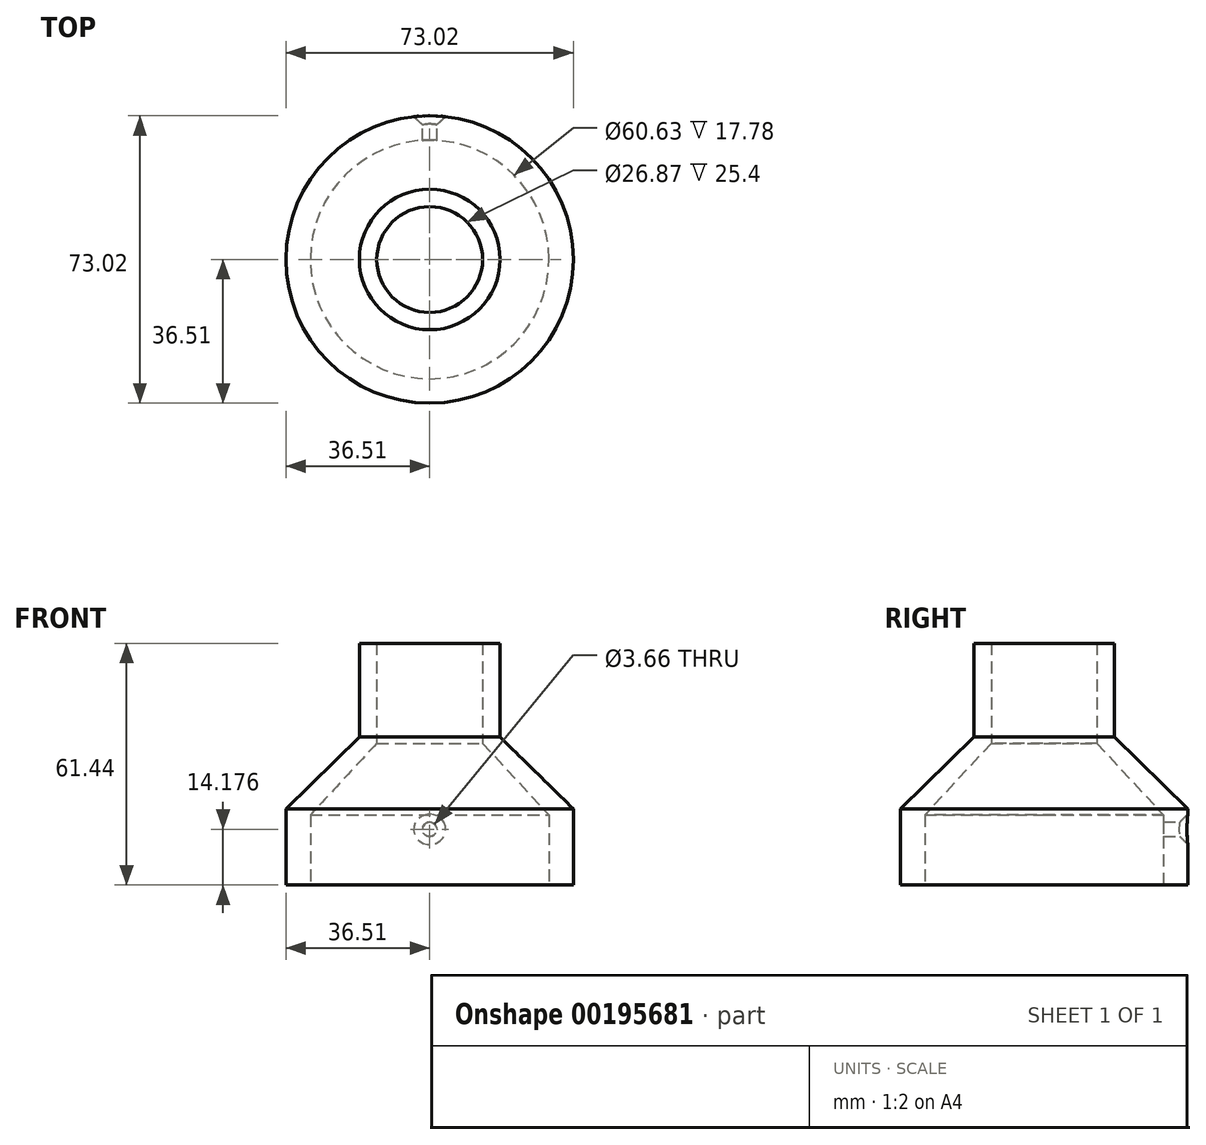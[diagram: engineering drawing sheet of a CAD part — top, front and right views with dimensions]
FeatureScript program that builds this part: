
annotation { "Feature Type Name" : "Feature", "Feature Type Description" : "" }
export const myFeature = defineFeature(function(context is Context, id is Id, definition is map)
    precondition{}
    {
        {
            var Q0;
            Q0=qCreatedBy(makeId("Top.planeOp"),FACE);
            var sketch = newSketch(context, id + "F0", { "sketchPlane" : qUnion([Q0])});
            skCircle(sketch, "E0", {"center": v(0, 0) * mm, "radius": 36.51 * mm});
            skSolve(sketch);
        }
        {
            var Q0;
            Q0 = qSketchRegion(id + "F0", true);
            extrude(context, id + "F1", {"entities" : qUnion([Q0]), "depth" : 39.69 * mm, "offsetDistance" : 25.4 * mm});
        }
        {
            var Q0;
            Q0=makeQuery(id+"F1.opExtrude","CAP_FACE",FACE,{"disambiguationData":[OSD([sQuery(id+"F0.wireOp",EDGE,"E0")])],"isStart":false});
            cPlane(context, id + "F2", {"entities" : qUnion([Q0]), "cplaneType" : CPlaneType.OFFSET, "offset" : 18.26 * mm, "width" : 152.4 * mm, "height" : 152.4 * mm});
        }
        {
            var Q0;
            Q0=qCreatedBy(id+"F2.planeOp",FACE);
            var sketch = newSketch(context, id + "F3", { "sketchPlane" : qUnion([Q0])});
            skCircle(sketch, "E1", {"center": v(0, 0) * mm, "radius": 17.86 * mm});
            skSolve(sketch);
        }
        {
            var Q0;
            Q0=makeQuery(id+"F1.opExtrude","CAP_FACE",FACE,{"disambiguationData":[OSD([sQuery(id+"F0.wireOp",EDGE,"E0")])],"isStart":false});
            var Q1;
            Q1=makeQuery(id+"F3.imprint","IMPRINT",FACE,{"disambiguationData":[TD([[makeQuery(id+"F3.imprint","IMPRINT",EDGE,{"derivedFrom":sQuery(id+"F3.wireOp",EDGE,"E1")}),1.0]])]});
            loft(context, id + "F4", {"operationType" : NewBodyOperationType.ADD, "sheetProfilesArray" : [{ "sheetProfileEntities" : qUnion([Q0]) }, { "sheetProfileEntities" : qUnion([Q1]) }]});
        }
        {
            var Q0;
            Q0=makeQuery(id+"F1.opExtrude","CAP_FACE",FACE,{"disambiguationData":[OSD([sQuery(id+"F0.wireOp",EDGE,"E0")])],"isStart":true});
            cPlane(context, id + "F5", {"entities" : qUnion([Q0]), "cplaneType" : CPlaneType.OFFSET, "offset" : 81.76 * mm, "oppositeDirection" : true, "width" : 152.4 * mm, "height" : 152.4 * mm});
        }
        {
            var Q0;
            Q0=makeQuery(id+"F4.opLoft","CAP_FACE",FACE,{"disambiguationData":[OSD([makeQuery(id+"F3.imprint","IMPRINT",FACE,{"disambiguationData":[TD([[makeQuery(id+"F3.imprint","IMPRINT",EDGE,{"derivedFrom":sQuery(id+"F3.wireOp",EDGE,"E1")}),1.0]])]})])],"isStart":true});
            var Q1;
            Q1=qCreatedBy(id+"F5.planeOp",FACE);
            extrude(context, id + "F6", {"entities" : qUnion([Q0]), "operationType" : NewBodyOperationType.ADD, "endBound" : BoundingType.UP_TO_SURFACE, "depth" : 25.4 * mm, "endBoundEntityFace" : qUnion([Q1]), "offsetDistance" : 25.4 * mm});
        }
        {
            var Q0;
            Q0=qCreatedBy(makeId("Front.planeOp"),FACE);
            var sketch = newSketch(context, id + "F7", { "sketchPlane" : qUnion([Q0])});
            skLineSegment(sketch, "E2.bottom", {"start": v(0, 81.76) * mm, "end": v(13.44, 81.76) * mm});
            skLineSegment(sketch, "E2.right", {"start": v(13.44, 81.76) * mm, "end": v(13.44, 56.36) * mm});
            skPoint(sketch, "E3", {"position": v(0, 81.76) * mm});
            skLineSegment(sketch, "E4", {"start": v(0, 81.76) * mm, "end": v(0, 0) * mm});
            skPoint(sketch, "E2.left.start.orphan", {"position": v(-13.44, 81.76) * mm});
            skLineSegment(sketch, "E5", {"start": v(0, 0) * mm, "end": v(30.31, 0) * mm});
            skLineSegment(sketch, "E6", {"start": v(30.31, 0) * mm, "end": v(30.31, 38.1) * mm});
            skLineSegment(sketch, "E7", {"start": v(13.44, 56.36) * mm, "end": v(30.31, 38.1) * mm});
            skSolve(sketch);
        }
        {
            var Q0;
            Q0 = qSketchRegion(id + "F7", true);
            var Q1;
            Q1 = qConstructionFilter(qBodyType(qCreatedBy(id + "F7" ,EDGE), BodyType.WIRE), ConstructionObject.NO);
            var Q2;
            Q2=sQuery(id+"F7.wireOp",EDGE,"E4");
            revolve(context, id + "F8", {"operationType" : NewBodyOperationType.REMOVE, "surfaceOperationType" : NewSurfaceOperationType.NEW, "entities" : qUnion([Q0]), "surfaceEntities" : qUnion([Q1]), "axis" : qUnion([Q2]), "revolveType" : RevolveType.FULL, "oppositeDirection" : true});
        }
        {
            var Q0;
            Q0=makeQuery(id+"F1.opExtrude","CAP_FACE",FACE,{"disambiguationData":[OSD([sQuery(id+"F0.wireOp",EDGE,"E0")])],"isStart":true});
            extrude(context, id + "F9", {"entities" : qUnion([Q0]), "operationType" : NewBodyOperationType.REMOVE, "oppositeDirection" : true, "depth" : 20.32 * mm, "offsetDistance" : 25.4 * mm});
        }
        {
            var Q0;
            Q0=qCreatedBy(makeId("Front.planeOp"),FACE);
            var sketch = newSketch(context, id + "F10", { "sketchPlane" : qUnion([Q0])});
            skPoint(sketch, "E8", {"position": v(0, 31.5) * mm});
            skSolve(sketch);
        }
        {
            var Q0;
            Q0=makeQuery(id+"F9.boolean.opBoolean","COPY",FACE,{"derivedFrom":makeQuery(id+"F9.opExtrude","CAP_FACE",FACE,{"disambiguationData":[OSD([sQuery(id+"F0.wireOp",EDGE,"E0")])],"isStart":false})});
            var sketch = newSketch(context, id + "F11", { "sketchPlane" : qUnion([Q0])});
            skPoint(sketch, "E9", {"position": v(0, -36.51) * mm});
            skSolve(sketch);
        }
        {
            var Q0;
            Q0=qCreatedBy(makeId("Front.planeOp"),FACE);
            var Q1;
            Q1=sQuery(id+"F11.wireOp",VERTEX,"E9");
            cPlane(context, id + "F12", {"entities" : qUnion([Q0, Q1]), "cplaneType" : CPlaneType.PLANE_POINT, "offset" : 25.4 * mm, "width" : 152.4 * mm, "height" : 152.4 * mm});
        }
        {
            var Q0;
            Q0=qCreatedBy(id+"F12.planeOp",FACE);
            var sketch = newSketch(context, id + "F13", { "sketchPlane" : qUnion([Q0])});
            skCircle(sketch, "E10", {"center": v(0, 34.5) * mm, "radius": 1.83 * mm});
            skSolve(sketch);
        }
        {
            var Q0;
            Q0 = qSketchRegion(id + "F13", true);
            extrude(context, id + "F14", {"entities" : qUnion([Q0]), "operationType" : NewBodyOperationType.REMOVE, "depth" : 25.4 * mm, "offsetDistance" : 25.4 * mm});
        }
        {
            var Q0;
            Q0=qCreatedBy(makeId("Front.planeOp"),FACE);
            var sketch = newSketch(context, id + "F15", { "sketchPlane" : qUnion([Q0])});
            skLineSegment(sketch, "E11", {"start": v(0, 0) * mm, "end": v(0, 68.75) * mm});
            skSolve(sketch);
        }
        {
            var Q0;
            Q0=makeQuery(id+"F14.boolean.opBoolean","INTERSECT",EDGE,{"derivedFrom":[makeQuery(id+"F1.opExtrude","SWEPT_FACE",FACE,{"disambiguationData":[OSD([sQuery(id+"F0.wireOp",EDGE,"E0")])]}),makeQuery(id+"F14.opExtrude","SWEPT_FACE",FACE,{"disambiguationData":[OSD([sQuery(id+"F13.wireOp",EDGE,"E10")])]})]});
            chamfer(context, id + "F16", {"entities" : qUnion([Q0]), "width" : 2.03 * mm, "tangentPropagation" : true});
        }
        {
            var Q0;
            Q0=qCreatedBy(makeId("Top.planeOp"),FACE);
            var Q1;
            Q1=sQuery(id+"F10.wireOp",VERTEX,"E8");
            cPlane(context, id + "F17", {"entities" : qUnion([Q0, Q1]), "cplaneType" : CPlaneType.PLANE_POINT, "offset" : 25.4 * mm, "width" : 152.4 * mm, "height" : 152.4 * mm});
        }
        {
            var Q0;
            Q0=qCreatedBy(id+"F17.planeOp",FACE);
            cPlane(context, id + "F18", {"entities" : qUnion([Q0]), "cplaneType" : CPlaneType.OFFSET, "offset" : 3 * mm, "width" : 152.4 * mm, "height" : 152.4 * mm});
        }
        {
            var Q0;
            Q0=qCreatedBy(id+"F18.planeOp",FACE);
            var sketch = newSketch(context, id + "F19", { "sketchPlane" : qUnion([Q0])});
            skPoint(sketch, "E12", {"position": v(0, 36.51) * mm});
            skPoint(sketch, "E13.1.0", {"position": v(-31.62, -18.26) * mm});
            skPoint(sketch, "E13.2.0", {"position": v(31.62, -18.26) * mm});
            skPoint(sketch, "E13.center", {"position": v(0, 0) * mm});
            skLineSegment(sketch, "E14", {"start": v(0, 0) * mm, "end": v(0, 36.51) * mm});
            skLineSegment(sketch, "E15", {"start": v(0, 0) * mm, "end": v(31.62, -18.26) * mm});
            skLineSegment(sketch, "E16", {"start": v(0, 0) * mm, "end": v(-31.62, -18.26) * mm});
            skSolve(sketch);
        }
    });
